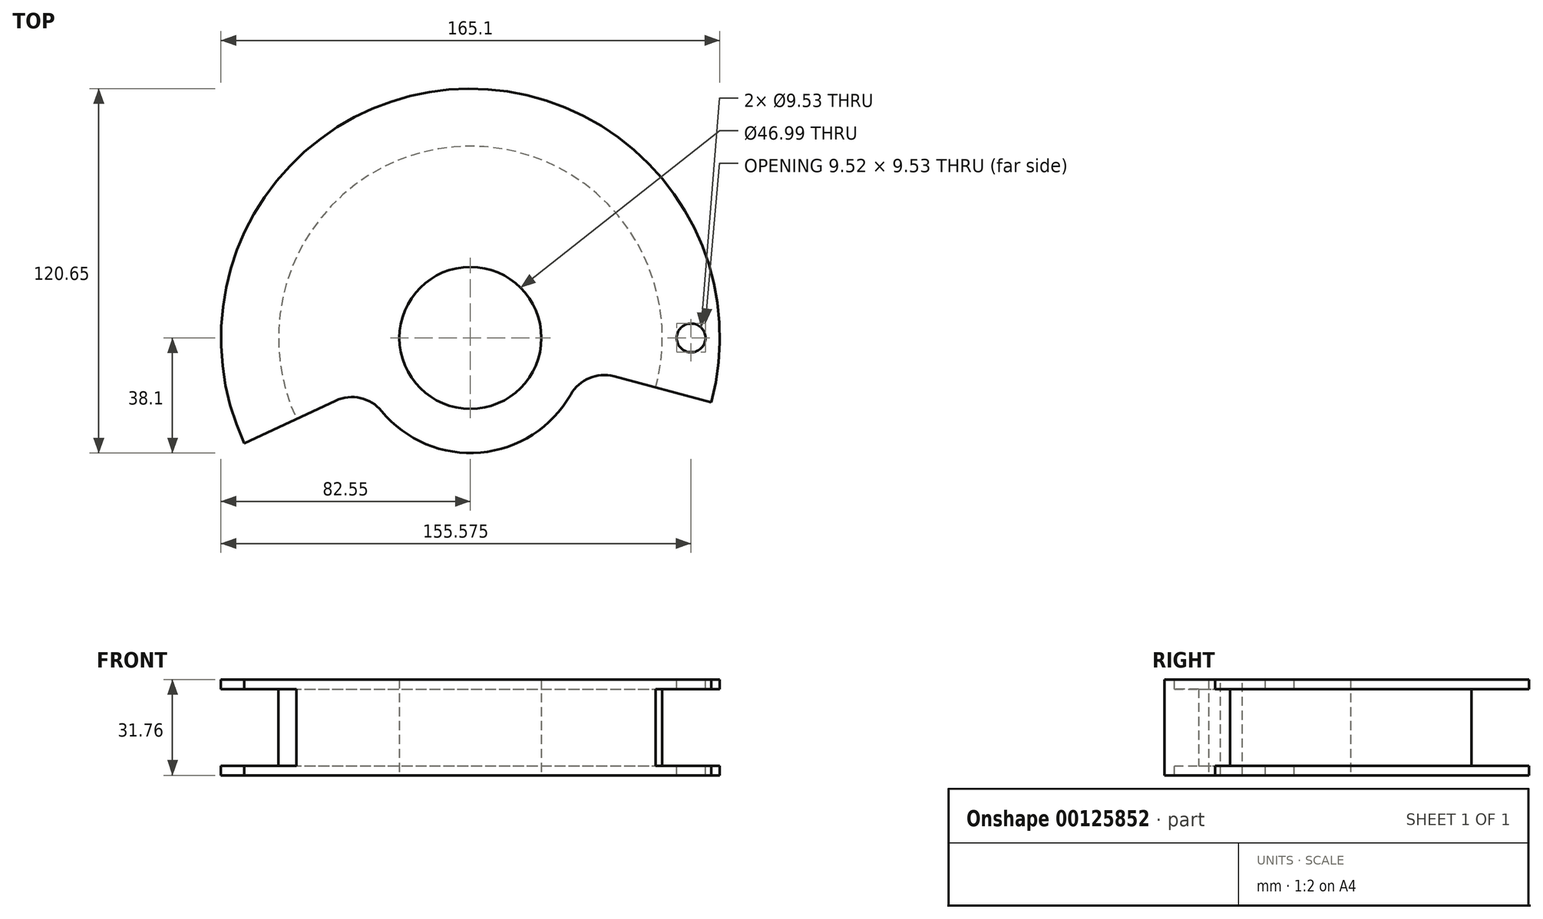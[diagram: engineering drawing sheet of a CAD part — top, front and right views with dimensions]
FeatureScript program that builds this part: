
annotation { "Feature Type Name" : "Feature", "Feature Type Description" : "" }
export const myFeature = defineFeature(function(context is Context, id is Id, definition is map)
    precondition{}
    {
        {
            var Q0;
            Q0=qCreatedBy(makeId("Front.planeOp"),FACE);
            var sketch = newSketch(context, id + "F0", { "sketchPlane" : qUnion([Q0])});
            skLineSegment(sketch, "E0", {"start": v(23.5, 15.87) * mm, "end": v(23.5, -15.87) * mm});
            skLineSegment(sketch, "E1", {"start": v(23.5, -15.88) * mm, "end": v(29.85, -15.88) * mm});
            skLineSegment(sketch, "E2", {"start": v(29.85, -15.88) * mm, "end": v(29.85, -15.88) * mm});
            skLineSegment(sketch, "E3", {"start": v(29.85, -15.88) * mm, "end": v(60.33, -15.87) * mm});
            skLineSegment(sketch, "E4", {"start": v(60.33, -15.87) * mm, "end": v(60.33, -15.87) * mm});
            skLineSegment(sketch, "E5", {"start": v(60.33, -15.87) * mm, "end": v(82.55, -15.87) * mm});
            skLineSegment(sketch, "E6", {"start": v(82.55, -15.87) * mm, "end": v(82.55, -12.7) * mm});
            skLineSegment(sketch, "E7", {"start": v(82.55, -12.7) * mm, "end": v(63.5, -12.7) * mm});
            skLineSegment(sketch, "E8", {"start": v(63.5, -12.7) * mm, "end": v(63.5, 12.7) * mm});
            skLineSegment(sketch, "E9", {"start": v(63.5, 12.7) * mm, "end": v(82.55, 12.7) * mm});
            skLineSegment(sketch, "E10", {"start": v(82.55, 12.7) * mm, "end": v(82.55, 15.88) * mm});
            skLineSegment(sketch, "E11", {"start": v(82.55, 15.88) * mm, "end": v(60.33, 15.88) * mm});
            skLineSegment(sketch, "E12", {"start": v(60.33, 15.88) * mm, "end": v(60.33, 15.88) * mm});
            skLineSegment(sketch, "E13", {"start": v(60.32, 15.88) * mm, "end": v(29.84, 15.88) * mm});
            skLineSegment(sketch, "E14", {"start": v(29.85, 15.88) * mm, "end": v(29.85, 15.88) * mm});
            skLineSegment(sketch, "E15", {"start": v(29.85, 15.88) * mm, "end": v(23.5, 15.87) * mm});
            skPoint(sketch, "E16", {"position": v(23.5, 0) * mm});
            skPoint(sketch, "E17", {"position": v(63.5, 0) * mm});
            skLineSegment(sketch, "E18", {"start": v(29.85, 15.88) * mm, "end": v(29.85, -15.88) * mm, "construction": true});
            skLineSegment(sketch, "E19", {"start": v(0, 0) * mm, "end": v(0, 34.47) * mm, "construction": true});
            skPoint(sketch, "E20", {"position": v(29.85, 0) * mm});
            skSolve(sketch);
        }
        {
            var Q0;
            Q0=makeQuery(id+"F0.imprint","IMPRINT",FACE,{"disambiguationData":[TD([[makeQuery(id+"F0.imprint","IMPRINT",EDGE,{"derivedFrom":sQuery(id+"F0.wireOp",EDGE,"E0")}),1.0]])]});
            var Q1;
            Q1=sQuery(id+"F0.wireOp",EDGE,"E19");
            revolve(context, id + "F1", {"entities" : qUnion([Q0]), "axis" : qUnion([Q1]), "revolveType" : RevolveType.FULL});
        }
        {
            var Q0;
            Q0=qCreatedBy(makeId("Top.planeOp"),FACE);
            var sketch = newSketch(context, id + "F2", { "sketchPlane" : qUnion([Q0])});
            skCircle(sketch, "E21.0", {"center": v(0, 0) * mm, "radius": 63.5 * mm, "construction": true});
            skCircle(sketch, "E22.1", {"center": v(0, 0) * mm, "radius": 82.55 * mm, "construction": true});
            skCircle(sketch, "E22.2", {"center": v(0, 0) * mm, "radius": 29.85 * mm, "construction": true});
            skCircle(sketch, "E22.3", {"center": v(0, 0) * mm, "radius": 82.55 * mm, "construction": true});
            skCircle(sketch, "E22.4", {"center": v(0, 0) * mm, "radius": 23.5 * mm, "construction": true});
            skCircle(sketch, "E22.6", {"center": v(0, 0) * mm, "radius": 60.33 * mm, "construction": true});
            skCircle(sketch, "E22.7", {"center": v(0, 0) * mm, "radius": 82.55 * mm, "construction": true});
            skCircle(sketch, "E22.9", {"center": v(0, 0) * mm, "radius": 23.5 * mm, "construction": true});
            skCircle(sketch, "E22.11", {"center": v(0, 0) * mm, "radius": 82.55 * mm, "construction": true});
            skCircle(sketch, "E22.13", {"center": v(0, 0) * mm, "radius": 29.85 * mm, "construction": true});
            skCircle(sketch, "E22.14", {"center": v(0, 0) * mm, "radius": 82.55 * mm, "construction": true});
            skCircle(sketch, "E22.15", {"center": v(0, 0) * mm, "radius": 60.33 * mm, "construction": true});
            skCircle(sketch, "E22.16", {"center": v(0, 0) * mm, "radius": 23.5 * mm, "construction": true});
            skLineSegment(sketch, "E23", {"start": v(63.5, 0) * mm, "end": v(82.55, 0) * mm, "construction": true});
            skPoint(sketch, "E24", {"position": v(73.03, 0) * mm});
            skCircle(sketch, "E25", {"center": v(73.03, 0) * mm, "radius": 4.76 * mm});
            skSolve(sketch);
        }
        {
            var Q0;
            Q0=makeQuery(id+"F2.imprint","IMPRINT",FACE,{"disambiguationData":[TD([[makeQuery(id+"F2.imprint","IMPRINT",EDGE,{"derivedFrom":sQuery(id+"F2.wireOp",EDGE,"E25")}),1.0]])]});
            extrude(context, id + "F3", {"entities" : qUnion([Q0]), "operationType" : NewBodyOperationType.REMOVE, "endBound" : BoundingType.SYMMETRIC, "oppositeDirection" : true, "depth" : 101.6 * mm});
        }
        {
            var Q0;
            Q0=makeQuery(id+"F1.opRevolve","SWEPT_FACE",FACE,{"disambiguationData":[OSD([sQuery(id+"F0.wireOp",EDGE,"E11")])]});
            var sketch = newSketch(context, id + "F4", { "sketchPlane" : qUnion([Q0])});
            skLineSegment(sketch, "E26", {"start": v(0, 0) * mm, "end": v(79.74, -21.37) * mm, "construction": true});
            skLineSegment(sketch, "E27", {"start": v(0, 0) * mm, "end": v(82.55, 0) * mm, "construction": true});
            skLineSegment(sketch, "E28", {"start": v(0, 0) * mm, "end": v(-74.82, -34.89) * mm, "construction": true});
            skCircle(sketch, "E29", {"center": v(0, 0) * mm, "radius": 38.1 * mm, "construction": true});
            skLineSegment(sketch, "E30", {"start": v(79.74, -21.37) * mm, "end": v(36.8, -9.86) * mm});
            skLineSegment(sketch, "E31", {"start": v(-74.82, -34.89) * mm, "end": v(-34.53, -16.1) * mm});
            skArc(sketch, "E32", {"start": v(-34.53, -16.1) * mm, "mid": v(3.32, -37.96) * mm, "end": v(36.8, -9.86) * mm});
            skSolve(sketch);
        }
        {
            var Q0;
            {var subQ0=sQuery(id+"F4.wireOp",EDGE,"E30");var subQ1=sQuery(id+"F0.wireOp",EDGE,"E11");var subQ2=makeQuery(id+"F1.opRevolve","SWEPT_EDGE",EDGE,{"disambiguationData":[OSD([sQuery(id+"F0.wireOp",EDGE,"E10"),subQ1])]});var subQ3=makeQuery(id+"F4.imprint","INTERSECT",VERTEX,{"derivedFrom":[subQ2,subQ0]});Q0=makeQuery(id+"F4.imprint","IMPRINT",FACE,{"disambiguationData":[TD([[makeQuery(id+"F4.imprint","IMPRINT",EDGE,{"disambiguationData":[TD([[subQ3,-1.0]])],"derivedFrom":subQ0}),1.0]])]});}
            var Q1;
            {var subQ0=sQuery(id+"F4.wireOp",EDGE,"E32");Q1=makeQuery(id+"F4.imprint","IMPRINT",FACE,{"disambiguationData":[TD([[makeQuery(id+"F4.imprint","IMPRINT",EDGE,{"derivedFrom":subQ0}),-1.0]])]});}
            extrude(context, id + "F5", {"entities" : qUnion([Q0, Q1]), "operationType" : NewBodyOperationType.REMOVE, "endBound" : BoundingType.THROUGH_ALL, "oppositeDirection" : true, "depth" : 25.4 * mm});
        }
        {
            var Q0;
            Q0=makeQuery(id+"F5.boolean.opBoolean","COPY",EDGE,{"derivedFrom":makeQuery(id+"F5.opExtrude","SWEPT_EDGE",EDGE,{"disambiguationData":[OSD([sQuery(id+"F4.wireOp",EDGE,"E31"),sQuery(id+"F4.wireOp",EDGE,"E32")])]})});
            var Q1;
            Q1=makeQuery(id+"F5.boolean.opBoolean","COPY",EDGE,{"derivedFrom":makeQuery(id+"F5.opExtrude","SWEPT_EDGE",EDGE,{"disambiguationData":[OSD([sQuery(id+"F4.wireOp",EDGE,"E30"),sQuery(id+"F4.wireOp",EDGE,"E32")])]})});
            fillet(context, id + "F6", {"entities" : qUnion([Q0, Q1]), "radius" : 12.7 * mm, "tangentPropagation" : true, "allowEdgeOverflow" : false});
        }
    });
